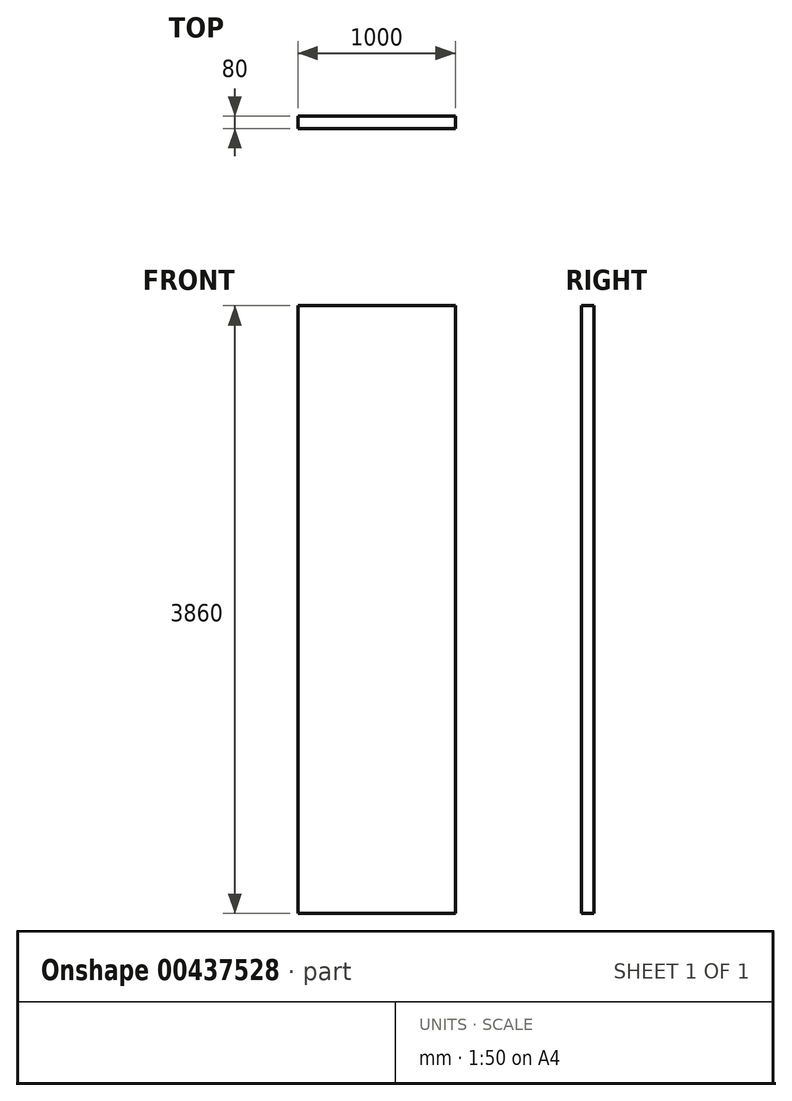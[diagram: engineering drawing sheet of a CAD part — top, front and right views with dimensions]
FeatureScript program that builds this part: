
annotation { "Feature Type Name" : "Feature", "Feature Type Description" : "" }
export const myFeature = defineFeature(function(context is Context, id is Id, definition is map)
    precondition{}
    {
        {
            var Q0;
            Q0=qCreatedBy(makeId("Front.planeOp"),FACE);
            var sketch = newSketch(context, id + "F0", { "sketchPlane" : qUnion([Q0])});
            skLineSegment(sketch, "E0.bottom", {"start": v(-500, 1930) * mm, "end": v(500, 1930) * mm});
            skLineSegment(sketch, "E0.top", {"start": v(-500, -1930) * mm, "end": v(500, -1930) * mm});
            skLineSegment(sketch, "E0.left", {"start": v(-500, 1930) * mm, "end": v(-500, -1930) * mm});
            skLineSegment(sketch, "E0.right", {"start": v(500, 1930) * mm, "end": v(500, -1930) * mm});
            skPoint(sketch, "E0.middle", {"position": v(0, 0) * mm});
            skSolve(sketch);
        }
        {
            var Q0;
            Q0=makeQuery(id+"F0.imprint","IMPRINT",FACE,{"disambiguationData":[TD([[makeQuery(id+"F0.imprint","IMPRINT",EDGE,{"derivedFrom":sQuery(id+"F0.wireOp",EDGE,"E0.bottom")}),-1.0]])]});
            extrude(context, id + "F1", {"entities" : qUnion([Q0]), "depth" : 80 * mm});
        }
    });
